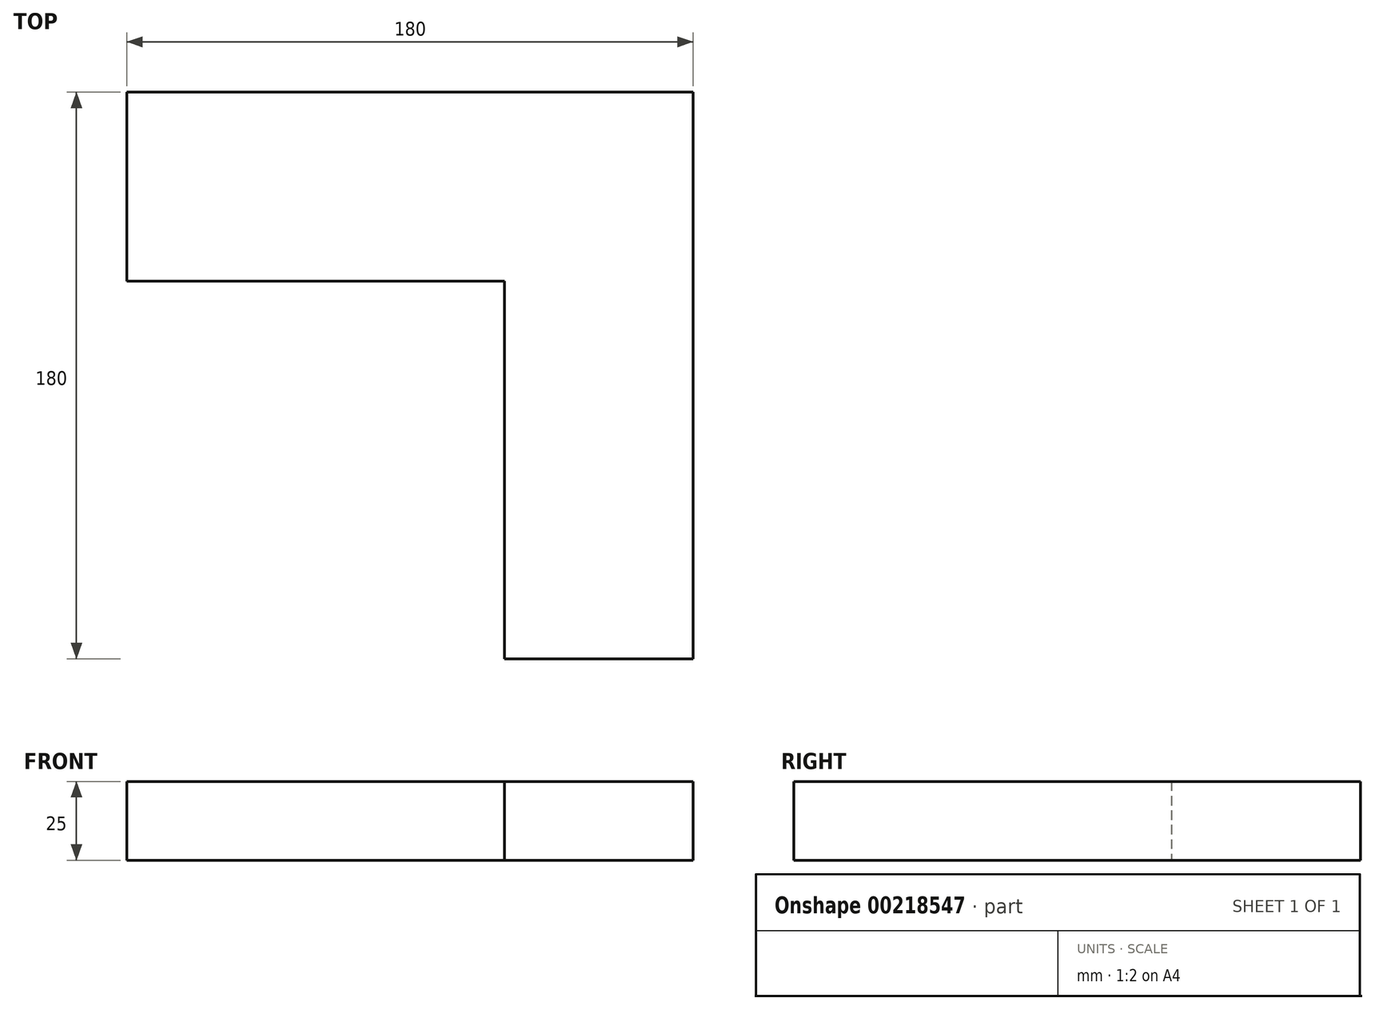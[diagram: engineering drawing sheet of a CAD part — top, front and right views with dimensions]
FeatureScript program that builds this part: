
annotation { "Feature Type Name" : "Feature", "Feature Type Description" : "" }
export const myFeature = defineFeature(function(context is Context, id is Id, definition is map)
    precondition{}
    {
        {
            assignVariable(context, id + "F0", {"name" : "thickness", "anyValue" : 25 * mm});
        }
        {
            var Q0;
            Q0=qCreatedBy(makeId("Top.planeOp"),FACE);
            var sketch = newSketch(context, id + "F1", { "sketchPlane" : qUnion([Q0])});
            skLineSegment(sketch, "E0.bottom", {"start": v(0, 0) * mm, "end": v(-120, 0) * mm});
            skLineSegment(sketch, "E0.top", {"start": v(60, 60) * mm, "end": v(-120, 60) * mm});
            skLineSegment(sketch, "E0.right", {"start": v(-120, 0) * mm, "end": v(-120, 60) * mm});
            skLineSegment(sketch, "E1", {"start": v(0, 0) * mm, "end": v(12.68, 12.68) * mm});
            skArc(sketch, "E2", {"start": v(33.66, 43.66) * mm, "mid": v(20, 40) * mm, "end": v(16.34, 26.34) * mm});
            skPoint(sketch, "E3", {"position": v(20, 20) * mm});
            skPoint(sketch, "E4", {"position": v(40, 40) * mm});
            skLineSegment(sketch, "E5.trimOffspring", {"start": v(47.32, 47.32) * mm, "end": v(60, 60) * mm});
            skArc(sketch, "E6.filletArc", {"start": v(12.68, 12.68) * mm, "mid": v(16.34, 19.02) * mm, "end": v(16.34, 26.34) * mm});
            skArc(sketch, "E7.filletArc", {"start": v(33.66, 43.66) * mm, "mid": v(40.98, 43.66) * mm, "end": v(47.32, 47.32) * mm});
            skSolve(sketch);
        }
        {
            var Q0;
            Q0=makeQuery(id+"F1.imprint","IMPRINT",FACE,{"disambiguationData":[TD([[makeQuery(id+"F1.imprint","IMPRINT",EDGE,{"derivedFrom":sQuery(id+"F1.wireOp",EDGE,"E0.bottom")}),-1.0]])]});
            extrude(context, id + "F2", {"entities" : qUnion([Q0]), "depth" : getVariable(context, 'thickness') / 2});
        }
        {
            var Q0;
            Q0=qCreatedBy(makeId("Top.planeOp"),FACE);
            var sketch = newSketch(context, id + "F3", { "sketchPlane" : qUnion([Q0])});
            skLineSegment(sketch, "E8.bottom", {"start": v(60, 0) * mm, "end": v(-120, 0) * mm});
            skLineSegment(sketch, "E8.top", {"start": v(60, 60) * mm, "end": v(-120, 60) * mm});
            skLineSegment(sketch, "E8.left", {"start": v(60, 0) * mm, "end": v(60, 60) * mm});
            skLineSegment(sketch, "E8.right", {"start": v(-120, 0) * mm, "end": v(-120, 60) * mm});
            skSolve(sketch);
        }
        {
            var Q0;
            Q0=qSketchRegion(id+"F3",true);
            extrude(context, id + "F4", {"entities" : qUnion([Q0]), "operationType" : NewBodyOperationType.ADD, "oppositeDirection" : true, "depth" : getVariable(context, 'thickness') / 2});
        }
        {
            var Q0;
            Q0=qCreatedBy(makeId("Top.planeOp"),FACE);
            var sketch = newSketch(context, id + "F5", { "sketchPlane" : qUnion([Q0])});
            skLineSegment(sketch, "E9.bottom", {"start": v(0, 60) * mm, "end": v(60, 60) * mm});
            skLineSegment(sketch, "E9.top", {"start": v(0, -120) * mm, "end": v(60, -120) * mm});
            skLineSegment(sketch, "E9.left", {"start": v(0, 60) * mm, "end": v(0, -120) * mm});
            skLineSegment(sketch, "E9.right", {"start": v(60, 60) * mm, "end": v(60, -120) * mm});
            skLineSegment(sketch, "E10", {"start": v(0, 0) * mm, "end": v(12.68, 12.68) * mm});
            skArc(sketch, "E11", {"start": v(33.66, 43.66) * mm, "mid": v(20, 40) * mm, "end": v(16.34, 26.34) * mm});
            skPoint(sketch, "E12", {"position": v(20, 20) * mm});
            skLineSegment(sketch, "E13.trimOffspring", {"start": v(47.32, 47.32) * mm, "end": v(60, 60) * mm});
            skArc(sketch, "E14.filletArc", {"start": v(12.68, 12.68) * mm, "mid": v(16.34, 19.02) * mm, "end": v(16.34, 26.34) * mm});
            skPoint(sketch, "E15.visualSharp", {"position": v(40, 40) * mm});
            skArc(sketch, "E15.filletArc", {"start": v(33.66, 43.66) * mm, "mid": v(40.98, 43.66) * mm, "end": v(47.32, 47.32) * mm});
            skSolve(sketch);
        }
        {
            var Q0;
            {var subQ0=sQuery(id+"F5.wireOp",EDGE,"E9.top");Q0=makeQuery(id+"F5.imprint","IMPRINT",FACE,{"disambiguationData":[TD([[makeQuery(id+"F5.imprint","IMPRINT",EDGE,{"derivedFrom":subQ0}),1.0]])]});}
            extrude(context, id + "F6", {"entities" : qUnion([Q0]), "depth" : getVariable(context, 'thickness') / 2});
        }
        {
            var Q0;
            Q0=makeQuery(id+"F6.opExtrude","CAP_FACE",FACE,{"disambiguationData":[OSD([sQuery(id+"F5.wireOp",EDGE,"E9.top"),sQuery(id+"F5.wireOp",EDGE,"E9.left"),sQuery(id+"F5.wireOp",EDGE,"E9.right"),sQuery(id+"F5.wireOp",EDGE,"E10"),sQuery(id+"F5.wireOp",EDGE,"E11"),sQuery(id+"F5.wireOp",EDGE,"E13.trimOffspring"),sQuery(id+"F5.wireOp",EDGE,"E14.filletArc"),sQuery(id+"F5.wireOp",EDGE,"E15.filletArc")])],"isStart":true});
            var sketch = newSketch(context, id + "F7", { "sketchPlane" : qUnion([Q0])});
            skLineSegment(sketch, "E16.bottom", {"start": v(0, 120) * mm, "end": v(60, 120) * mm});
            skLineSegment(sketch, "E16.top", {"start": v(0, 0) * mm, "end": v(60, 0) * mm});
            skLineSegment(sketch, "E16.left", {"start": v(0, 120) * mm, "end": v(0, 0) * mm});
            skLineSegment(sketch, "E16.right", {"start": v(60, 120) * mm, "end": v(60, 0) * mm});
            skSolve(sketch);
        }
        {
            var Q0;
            Q0=makeQuery(id+"F7.imprint","IMPRINT",FACE,{"disambiguationData":[TD([[makeQuery(id+"F7.imprint","IMPRINT",EDGE,{"derivedFrom":sQuery(id+"F7.wireOp",EDGE,"E16.bottom")}),-1.0]])]});
            extrude(context, id + "F8", {"entities" : qUnion([Q0]), "operationType" : NewBodyOperationType.ADD, "depth" : getVariable(context, 'thickness') / 2});
        }
    });
